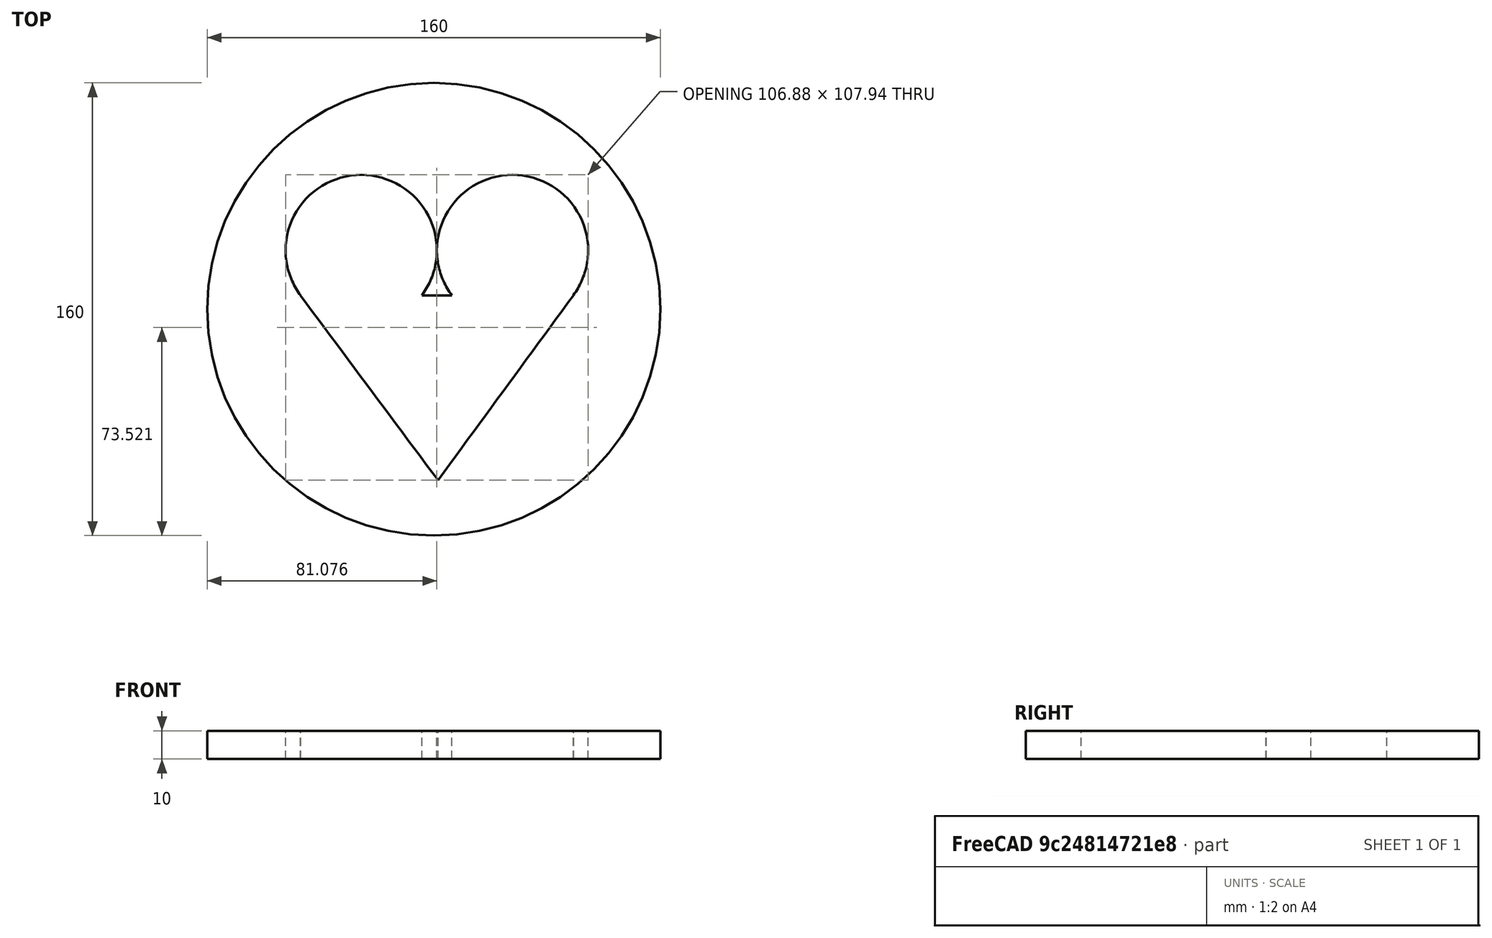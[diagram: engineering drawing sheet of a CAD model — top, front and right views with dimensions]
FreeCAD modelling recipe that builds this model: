
FCSTD DOCUMENT  (FreeCAD 0.21R33694 (Git))
Label: Solución Reto 1
License: All rights reserved
LicenseURL: http://en.wikipedia.org/wiki/All_rights_reserved
objects: Part::Feature×1, Part::Extrusion×1, Part::Cylinder×1, Part::Cut×1
note: 4 computed .brp shape members not serialized (recipe doc carries the construction recipe); baked Part::Feature solids carry a one-line shape summary decoded from their .brp

FEATURE [Part::Feature] path1
  shape: bbox 106.9 x 107.9 x 2e-07 mm, 0 faces, 0 solids (baked)
FEATURE [Part::Extrusion] Extrude
  Base = -> path1
  Dir = (0,0,1)
  DirMode = 2
  FaceMakerClass = Part::FaceMakerBullseye
  LengthFwd = 50
  LengthRev = 0
  Placement = pos=(-59,182,-21) rot=(0,0,1;0rad)
  Solid = true
  Symmetric = false
FEATURE [Part::Cylinder] Cylinder  label="Cilindro"
  Angle = 360
  AttacherType = Attacher::AttachEngine3D
  FirstAngle = 0
  Height = 10
  Placement = pos=(81,80,0) rot=(0,0,1;0rad)
  Radius = 80
  SecondAngle = 0
FEATURE [Part::Cut] Cut
  Base = -> Cylinder
  Refine = true
  Tool = -> Extrude
